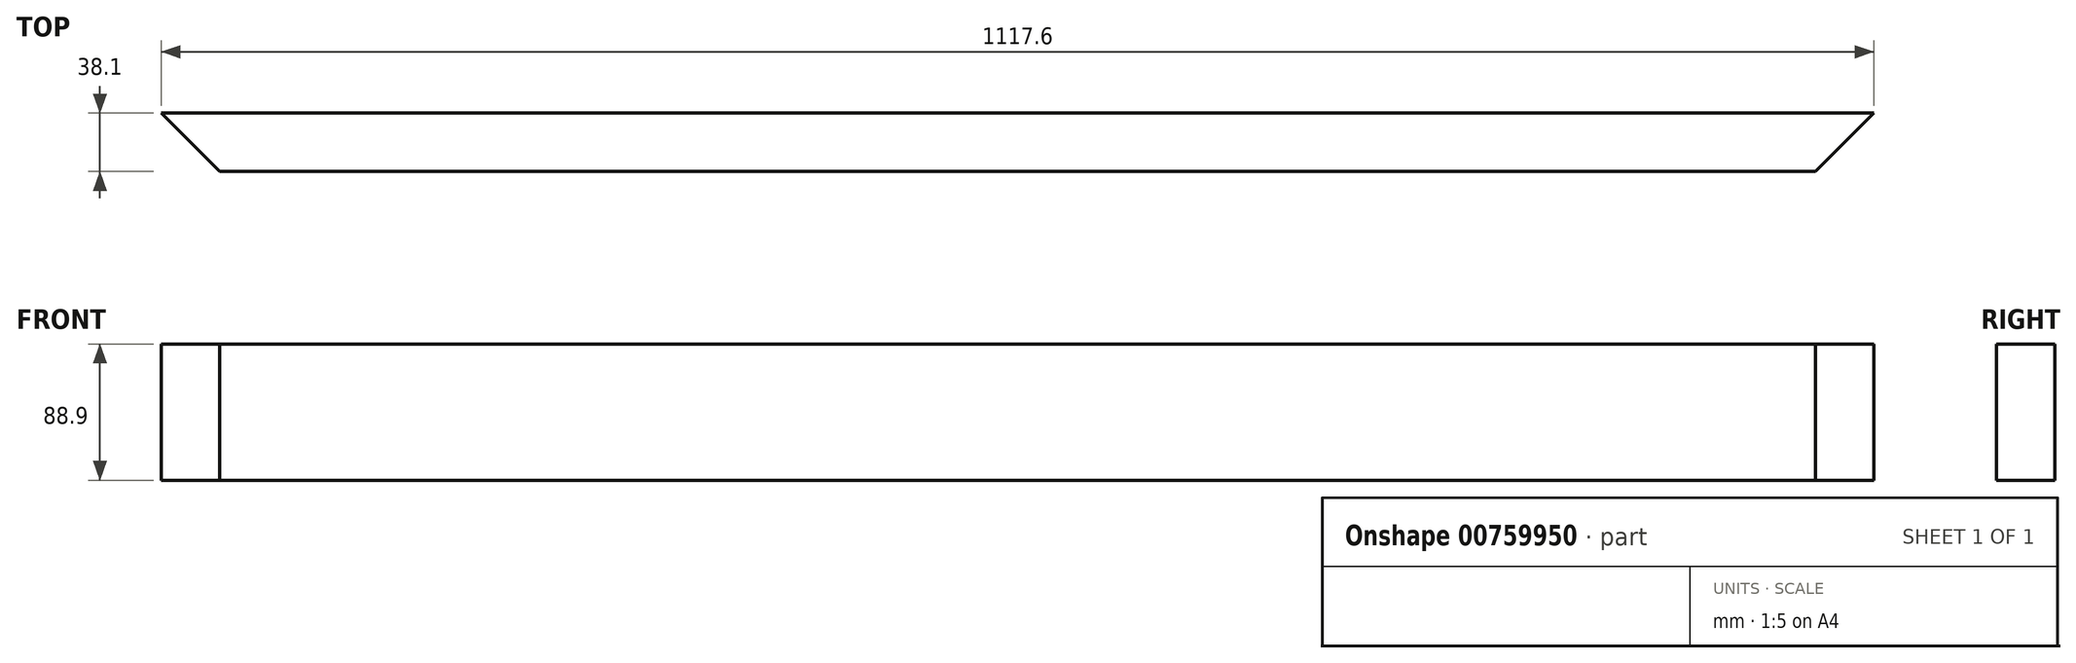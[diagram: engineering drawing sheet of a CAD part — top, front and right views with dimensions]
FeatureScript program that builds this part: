
annotation { "Feature Type Name" : "Feature", "Feature Type Description" : "" }
export const myFeature = defineFeature(function(context is Context, id is Id, definition is map)
    precondition{}
    {
        {
            var Q0;
            Q0=qCreatedBy(makeId("Top.planeOp"),FACE);
            var sketch = newSketch(context, id + "F0", { "sketchPlane" : qUnion([Q0])});
            skLineSegment(sketch, "E0", {"start": v(0, 38.1) * mm, "end": v(-1117.6, 38.1) * mm});
            skLineSegment(sketch, "E1", {"start": v(-1117.6, 38.1) * mm, "end": v(-1079.5, 0) * mm});
            skLineSegment(sketch, "E2", {"start": v(-1079.5, 0) * mm, "end": v(-38.1, 0) * mm});
            skLineSegment(sketch, "E3", {"start": v(-38.1, 0) * mm, "end": v(0, 38.1) * mm});
            skSolve(sketch);
        }
        {
            var Q0;
            Q0 = qSketchRegion(id + "F0", true);
            extrude(context, id + "F1", {"entities" : qUnion([Q0]), "oppositeDirection" : true, "depth" : 88.9 * mm, "offsetDistance" : 25.4 * mm});
        }
    });
